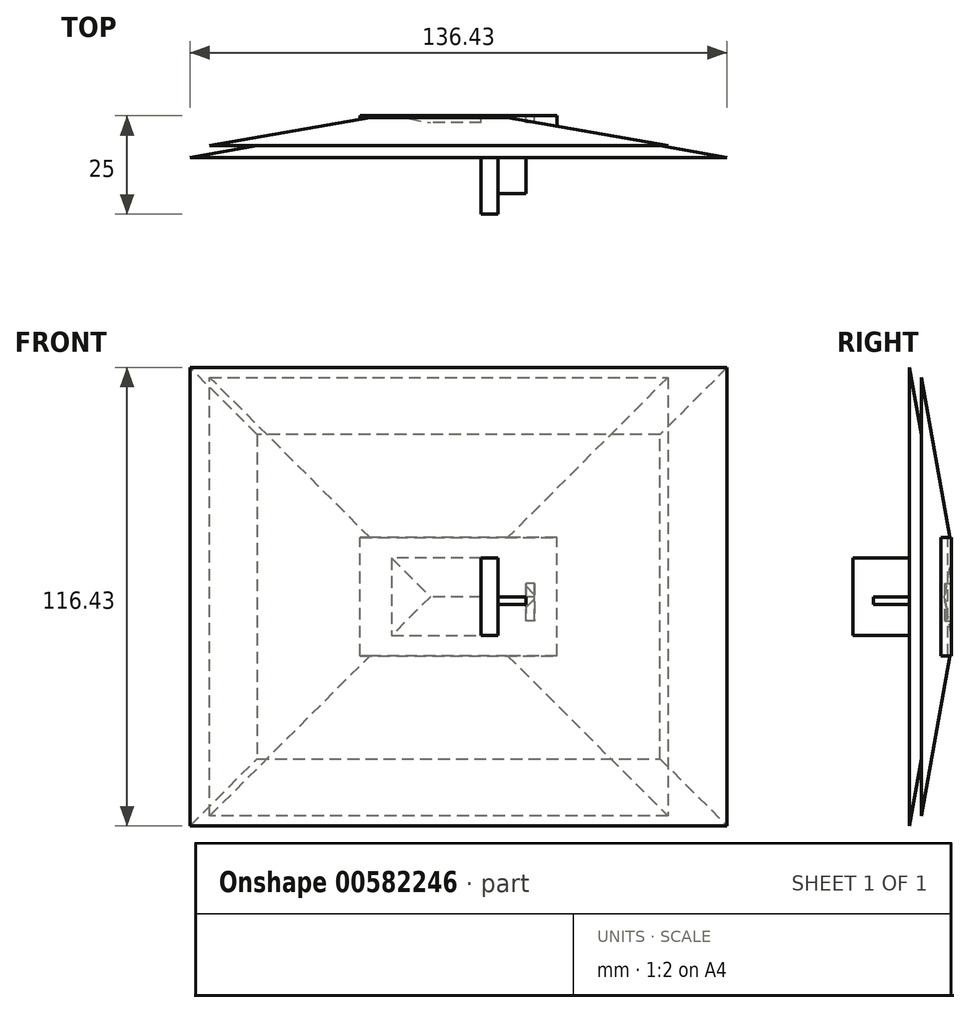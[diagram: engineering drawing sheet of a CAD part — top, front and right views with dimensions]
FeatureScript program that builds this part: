
annotation { "Feature Type Name" : "Feature", "Feature Type Description" : "" }
export const myFeature = defineFeature(function(context is Context, id is Id, definition is map)
    precondition{}
    {
        {
            var Q0;
            Q0=qCreatedBy(makeId("Front.planeOp"),FACE);
            var sketch = newSketch(context, id + "F0", { "sketchPlane" : qUnion([Q0])});
            skLineSegment(sketch, "E0.bottom", {"start": v(-46.12, -27.42) * mm, "end": v(3.88, -27.42) * mm});
            skLineSegment(sketch, "E0.top", {"start": v(-46.12, -57.42) * mm, "end": v(3.88, -57.42) * mm});
            skLineSegment(sketch, "E0.left", {"start": v(-46.12, -27.42) * mm, "end": v(-46.12, -57.42) * mm});
            skLineSegment(sketch, "E0.right", {"start": v(3.88, -27.42) * mm, "end": v(3.88, -57.42) * mm});
            skLineSegment(sketch, "E1.bottom", {"start": v(-41.12, -29.92) * mm, "end": v(-11.12, -29.92) * mm});
            skLineSegment(sketch, "E1.top", {"start": v(-41.12, -54.92) * mm, "end": v(-11.12, -54.92) * mm});
            skLineSegment(sketch, "E1.left", {"start": v(-41.12, -29.92) * mm, "end": v(-41.12, -54.92) * mm});
            skLineSegment(sketch, "E1.right", {"start": v(-11.12, -29.92) * mm, "end": v(-11.12, -54.92) * mm});
            skLineSegment(sketch, "E2.bottom", {"start": v(-38.12, -32.6) * mm, "end": v(-15.4, -32.6) * mm});
            skLineSegment(sketch, "E2.top", {"start": v(-38.12, -52.29) * mm, "end": v(-15.4, -52.29) * mm});
            skLineSegment(sketch, "E2.left", {"start": v(-38.12, -32.6) * mm, "end": v(-38.12, -52.29) * mm});
            skLineSegment(sketch, "E2.right", {"start": v(-15.4, -32.6) * mm, "end": v(-15.4, -52.29) * mm});
            skLineSegment(sketch, "E3.bottom", {"start": v(-15.4, -32.6) * mm, "end": v(-11.12, -32.6) * mm});
            skLineSegment(sketch, "E3.top", {"start": v(-15.4, -52.29) * mm, "end": v(-11.12, -52.29) * mm});
            skLineSegment(sketch, "E3.right", {"start": v(-11.12, -32.6) * mm, "end": v(-11.12, -52.29) * mm});
            skLineSegment(sketch, "E4.bottom", {"start": v(-11.12, -42.45) * mm, "end": v(-4.03, -42.45) * mm});
            skLineSegment(sketch, "E4.top", {"start": v(-11.12, -44.35) * mm, "end": v(-4.03, -44.35) * mm});
            skLineSegment(sketch, "E4.left", {"start": v(-11.12, -42.45) * mm, "end": v(-11.12, -44.35) * mm});
            skLineSegment(sketch, "E4.right", {"start": v(-4.03, -42.45) * mm, "end": v(-4.03, -44.35) * mm});
            skLineSegment(sketch, "E5.bottom", {"start": v(-4.03, -39.02) * mm, "end": v(-1.82, -39.02) * mm});
            skLineSegment(sketch, "E5.top", {"start": v(-4.03, -48.54) * mm, "end": v(-1.82, -48.54) * mm});
            skLineSegment(sketch, "E5.left", {"start": v(-4.03, -39.02) * mm, "end": v(-4.03, -48.54) * mm});
            skLineSegment(sketch, "E5.right", {"start": v(-1.82, -39.02) * mm, "end": v(-1.82, -48.54) * mm});
            skLineSegment(sketch, "E6.bottom", {"start": v(-36.17, -35.26) * mm, "end": v(-17.7, -35.26) * mm});
            skLineSegment(sketch, "E6.top", {"start": v(-36.17, -49.22) * mm, "end": v(-17.7, -49.22) * mm});
            skLineSegment(sketch, "E6.left", {"start": v(-36.17, -35.26) * mm, "end": v(-36.17, -49.22) * mm});
            skLineSegment(sketch, "E6.right", {"start": v(-17.7, -35.26) * mm, "end": v(-17.7, -49.22) * mm});
            skSolve(sketch);
        }
        {
            var Q0;
            Q0=makeQuery(id+"F0.imprint","IMPRINT",FACE,{"disambiguationData":[TD([[makeQuery(id+"F0.imprint","IMPRINT",EDGE,{"derivedFrom":sQuery(id+"F0.wireOp",EDGE,"E0.bottom")}),-1.0]])]});
            extrude(context, id + "F1", {"entities" : qUnion([Q0]), "depth" : 3 * mm, "offsetDistance" : 25.4 * mm});
        }
        {
            var Q0;
            Q0=makeQuery(id+"F0.imprint","IMPRINT",FACE,{"disambiguationData":[TD([[makeQuery(id+"F0.imprint","IMPRINT",EDGE,{"derivedFrom":sQuery(id+"F0.wireOp",EDGE,"E3.bottom")}),-1.0]])]});
            extrude(context, id + "F2", {"entities" : qUnion([Q0]), "operationType" : NewBodyOperationType.ADD, "depth" : 25 * mm, "offsetDistance" : 25.4 * mm});
        }
        {
            var Q0;
            {var subQ0=sQuery(id+"F0.wireOp",EDGE,"E4.bottom");Q0=makeQuery(id+"F0.imprint","IMPRINT",FACE,{"disambiguationData":[TD([[makeQuery(id+"F0.imprint","IMPRINT",EDGE,{"derivedFrom":subQ0}),-1.0]])]});}
            extrude(context, id + "F3", {"entities" : qUnion([Q0]), "operationType" : NewBodyOperationType.ADD, "depth" : 19.8 * mm, "offsetDistance" : 25.4 * mm});
        }
        {
            var Q0;
            {var subQ1=sQuery(id+"F0.wireOp",EDGE,"E1.bottom");Q0=makeQuery(id+"F0.imprint","IMPRINT",FACE,{"disambiguationData":[TD([[makeQuery(id+"F0.imprint","IMPRINT",EDGE,{"derivedFrom":subQ1}),-1.0]])]});}
            var Q1;
            Q1=makeQuery(id+"F1.opExtrude","CAP_FACE",FACE,{"disambiguationData":[OSD([sQuery(id+"F0.wireOp",EDGE,"E0.bottom"),sQuery(id+"F0.wireOp",EDGE,"E0.top"),sQuery(id+"F0.wireOp",EDGE,"E0.left"),sQuery(id+"F0.wireOp",EDGE,"E0.right"),sQuery(id+"F0.wireOp",EDGE,"E1.bottom"),sQuery(id+"F0.wireOp",EDGE,"E1.top"),sQuery(id+"F0.wireOp",EDGE,"E1.left"),sQuery(id+"F0.wireOp",EDGE,"E1.right"),sQuery(id+"F0.wireOp",EDGE,"E3.right"),sQuery(id+"F0.wireOp",EDGE,"E4.bottom"),sQuery(id+"F0.wireOp",EDGE,"E4.top"),sQuery(id+"F0.wireOp",EDGE,"E5.bottom"),sQuery(id+"F0.wireOp",EDGE,"E5.top"),sQuery(id+"F0.wireOp",EDGE,"E5.left"),sQuery(id+"F0.wireOp",EDGE,"E5.right")])],"isStart":false});
            extrude(context, id + "F4", {"entities" : qUnion([Q0, Q1]), "operationType" : NewBodyOperationType.ADD, "depth" : 7.62 * mm, "offsetDistance" : 25.4 * mm, "hasDraft" : true, "draftAngle" : 80 * degree});
        }
    });
